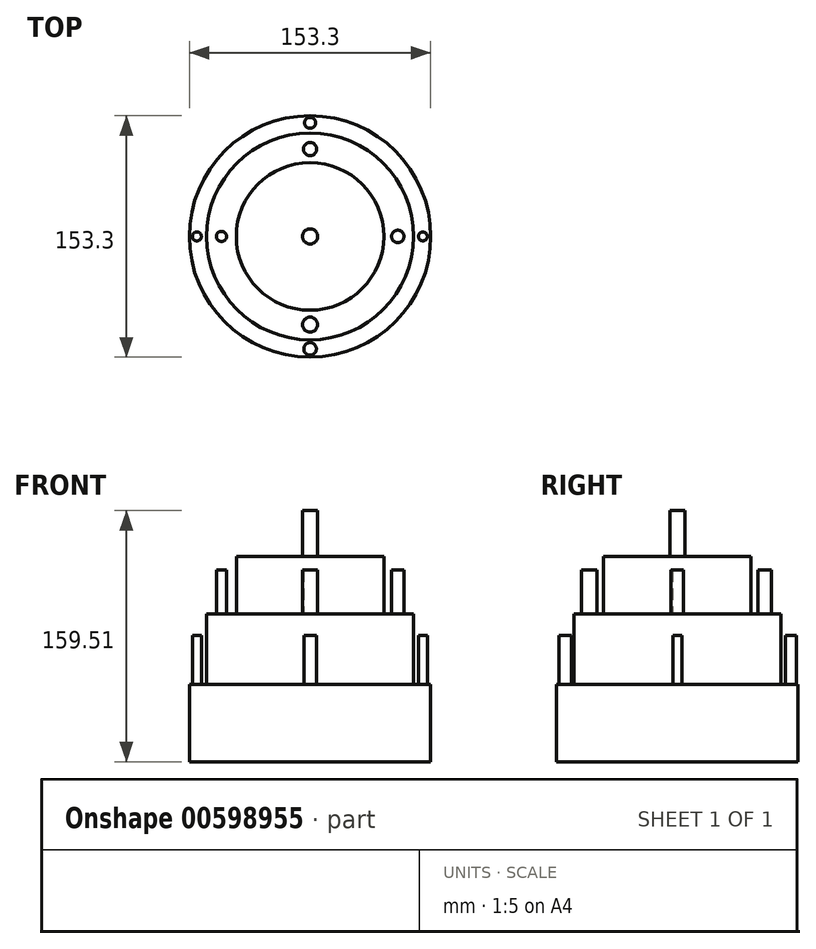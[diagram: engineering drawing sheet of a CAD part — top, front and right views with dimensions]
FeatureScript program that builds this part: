
annotation { "Feature Type Name" : "Feature", "Feature Type Description" : "" }
export const myFeature = defineFeature(function(context is Context, id is Id, definition is map)
    precondition{}
    {
        {
            var Q0;
            Q0=qCreatedBy(makeId("Top.planeOp"),FACE);
            var sketch = newSketch(context, id + "F0", { "sketchPlane" : qUnion([Q0])});
            skCircle(sketch, "E0", {"center": v(0, 0) * mm, "radius": 76.65 * mm});
            skSolve(sketch);
        }
        {
            var Q0;
            Q0 = qSketchRegion(id + "F0", true);
            extrude(context, id + "F1", {"entities" : qUnion([Q0]), "depth" : 49.02 * mm, "offsetDistance" : 25.4 * mm});
        }
        {
            var Q0;
            Q0=qCreatedBy(makeId("Top.planeOp"),FACE);
            var sketch = newSketch(context, id + "F2", { "sketchPlane" : qUnion([Q0])});
            skCircle(sketch, "E1", {"center": v(0, 0) * mm, "radius": 65.68 * mm});
            skSolve(sketch);
        }
        {
            var Q0;
            Q0 = qSketchRegion(id + "F2", true);
            extrude(context, id + "F3", {"entities" : qUnion([Q0]), "operationType" : NewBodyOperationType.ADD, "depth" : 93.98 * mm, "offsetDistance" : 25.4 * mm});
        }
        {
            var Q0;
            Q0=qCreatedBy(makeId("Top.planeOp"),FACE);
            var sketch = newSketch(context, id + "F4", { "sketchPlane" : qUnion([Q0])});
            skCircle(sketch, "E2", {"center": v(0, 0) * mm, "radius": 46.85 * mm});
            skSolve(sketch);
        }
        {
            var Q0;
            Q0 = qSketchRegion(id + "F4", true);
            extrude(context, id + "F5", {"entities" : qUnion([Q0]), "operationType" : NewBodyOperationType.ADD, "depth" : 130.3 * mm, "offsetDistance" : 25.4 * mm});
        }
        {
            var Q0;
            Q0=qCreatedBy(makeId("Top.planeOp"),FACE);
            var sketch = newSketch(context, id + "F6", { "sketchPlane" : qUnion([Q0])});
            skCircle(sketch, "E3", {"center": v(-71.9, 0) * mm, "radius": 2.88 * mm});
            skCircle(sketch, "E4", {"center": v(71.64, 0) * mm, "radius": 2.81 * mm});
            skCircle(sketch, "E5", {"center": v(0, 72.15) * mm, "radius": 3.47 * mm});
            skCircle(sketch, "E6", {"center": v(0, -71.38) * mm, "radius": 3.98 * mm});
            skSolve(sketch);
        }
        {
            var Q0;
            Q0 = qSketchRegion(id + "F6", true);
            extrude(context, id + "F7", {"entities" : qUnion([Q0]), "operationType" : NewBodyOperationType.ADD, "depth" : 80.26 * mm, "offsetDistance" : 25.4 * mm});
        }
        {
            var Q0;
            Q0=qCreatedBy(makeId("Top.planeOp"),FACE);
            var sketch = newSketch(context, id + "F8", { "sketchPlane" : qUnion([Q0])});
            skCircle(sketch, "E7", {"center": v(-56.26, 0) * mm, "radius": 3.23 * mm});
            skCircle(sketch, "E8", {"center": v(55.75, 0) * mm, "radius": 3.95 * mm});
            skCircle(sketch, "E9", {"center": v(0, -56) * mm, "radius": 4.77 * mm});
            skCircle(sketch, "E10", {"center": v(0, 55.5) * mm, "radius": 4.24 * mm});
            skCircle(sketch, "E11", {"center": v(0, 0) * mm, "radius": 3.4 * mm});
            skSolve(sketch);
        }
        {
            var Q0;
            Q0 = qSketchRegion(id + "F8", true);
            extrude(context, id + "F9", {"entities" : qUnion([Q0]), "operationType" : NewBodyOperationType.ADD, "depth" : 121.67 * mm, "offsetDistance" : 25.4 * mm});
        }
        {
            var Q0;
            Q0=qCreatedBy(makeId("Top.planeOp"),FACE);
            var sketch = newSketch(context, id + "F10", { "sketchPlane" : qUnion([Q0])});
            skCircle(sketch, "E12", {"center": v(0, 0) * mm, "radius": 4.83 * mm});
            skSolve(sketch);
        }
        {
            var Q0;
            Q0 = qSketchRegion(id + "F10", true);
            extrude(context, id + "F11", {"entities" : qUnion([Q0]), "operationType" : NewBodyOperationType.ADD, "depth" : 159.5 * mm, "offsetDistance" : 25.4 * mm});
        }
    });
